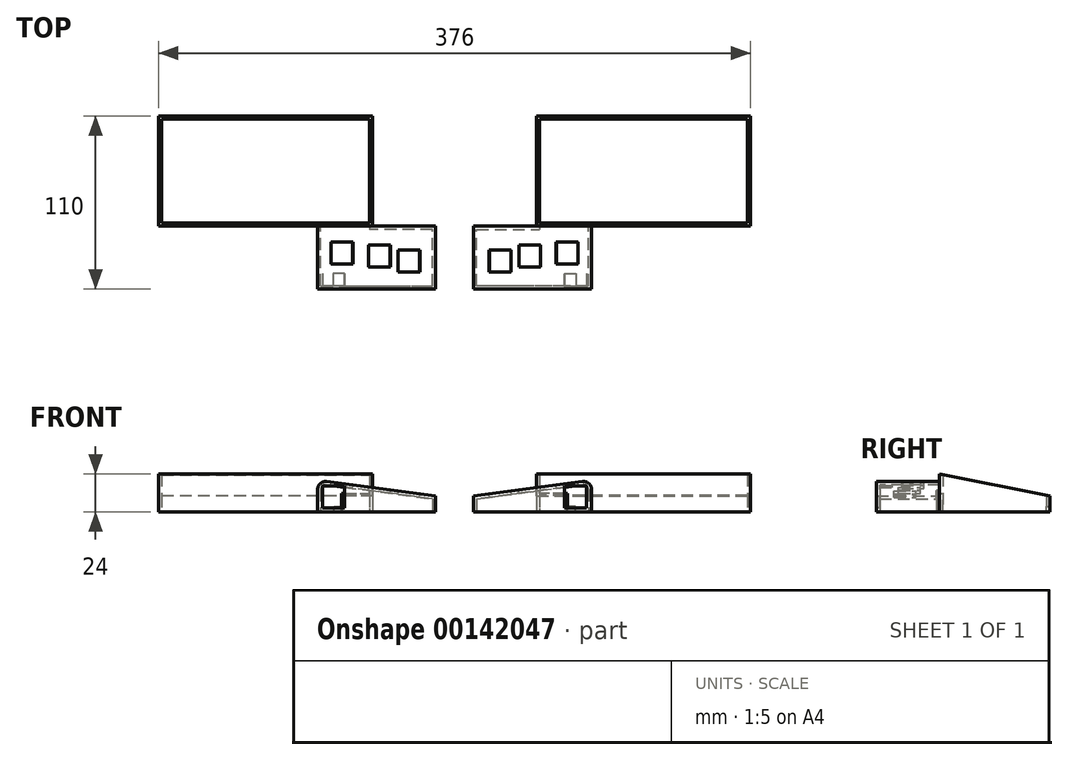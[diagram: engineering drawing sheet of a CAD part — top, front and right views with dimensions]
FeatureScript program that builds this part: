
annotation { "Feature Type Name" : "Feature", "Feature Type Description" : "" }
export const myFeature = defineFeature(function(context is Context, id is Id, definition is map)
    precondition{}
    {
        {
            var Q0;
            Q0=qCreatedBy(makeId("Top.planeOp"),FACE);
            var sketch = newSketch(context, id + "F0", { "sketchPlane" : qUnion([Q0])});
            skLineSegment(sketch, "E0.bottom", {"start": v(68, -35) * mm, "end": v(-68, -35) * mm});
            skLineSegment(sketch, "E0.top", {"start": v(68, 35) * mm, "end": v(-68, 35) * mm});
            skLineSegment(sketch, "E0.left", {"start": v(68, -35) * mm, "end": v(68, 35) * mm});
            skLineSegment(sketch, "E0.right", {"start": v(-68, -35) * mm, "end": v(-68, 35) * mm});
            skPoint(sketch, "E0.middle", {"position": v(0, 0) * mm});
            skLineSegment(sketch, "E1.bottom", {"start": v(-66, 35) * mm, "end": v(66, 35) * mm});
            skLineSegment(sketch, "E1.top", {"start": v(-66, -33) * mm, "end": v(66, -33) * mm});
            skLineSegment(sketch, "E1.left", {"start": v(-66, 35) * mm, "end": v(-66, -33) * mm});
            skLineSegment(sketch, "E1.right", {"start": v(66, 35) * mm, "end": v(66, -33) * mm});
            skLineSegment(sketch, "E2", {"start": v(-68, 4.76) * mm, "end": v(-66, 4.76) * mm});
            skPoint(sketch, "E2.endSnap0", {"position": v(-66, 1) * mm});
            skLineSegment(sketch, "E3", {"start": v(-7.66, -35) * mm, "end": v(-7.66, -33) * mm});
            skLineSegment(sketch, "E4", {"start": v(66, 1) * mm, "end": v(68, 1) * mm});
            skLineSegment(sketch, "E5", {"start": v(-66, 33) * mm, "end": v(66, 33) * mm});
            skLineSegment(sketch, "E6", {"start": v(0, 35) * mm, "end": v(0, 33) * mm});
            skLineSegment(sketch, "E7", {"start": v(-81.81, -13.23) * mm, "end": v(-79.54, -15.2) * mm});
            skLineSegment(sketch, "E8", {"start": v(-140.33, 40.9) * mm, "end": v(-140.33, -57.97) * mm});
            skSolve(sketch);
        }
        {
            var Q0;
            {var subQ3=sQuery(id+"F0.wireOp",EDGE,"E2");Q0=makeQuery(id+"F0.imprint","IMPRINT",FACE,{"disambiguationData":[TD([[makeQuery(id+"F0.imprint","IMPRINT",EDGE,{"derivedFrom":subQ3}),-1.0]])]});}
            var Q1;
            {var subQ5=sQuery(id+"F0.wireOp",EDGE,"E2");Q1=makeQuery(id+"F0.imprint","IMPRINT",FACE,{"disambiguationData":[TD([[makeQuery(id+"F0.imprint","IMPRINT",EDGE,{"derivedFrom":subQ5}),1.0]])]});}
            var Q2;
            {var subQ4=sQuery(id+"F0.wireOp",EDGE,"E3");Q2=makeQuery(id+"F0.imprint","IMPRINT",FACE,{"disambiguationData":[TD([[makeQuery(id+"F0.imprint","IMPRINT",EDGE,{"derivedFrom":subQ4}),-1.0]])]});}
            var Q3;
            {var subQ5=sQuery(id+"F0.wireOp",EDGE,"E4");Q3=makeQuery(id+"F0.imprint","IMPRINT",FACE,{"disambiguationData":[TD([[makeQuery(id+"F0.imprint","IMPRINT",EDGE,{"derivedFrom":subQ5}),1.0]])]});}
            var Q4;
            {var subQ3=sQuery(id+"F0.wireOp",EDGE,"E6");Q4=makeQuery(id+"F0.imprint","IMPRINT",FACE,{"disambiguationData":[TD([[makeQuery(id+"F0.imprint","IMPRINT",EDGE,{"derivedFrom":subQ3}),-1.0]])]});}
            var Q5;
            {var subQ3=sQuery(id+"F0.wireOp",EDGE,"E6");Q5=makeQuery(id+"F0.imprint","IMPRINT",FACE,{"disambiguationData":[TD([[makeQuery(id+"F0.imprint","IMPRINT",EDGE,{"derivedFrom":subQ3}),1.0]])]});}
            extrude(context, id + "F1", {"entities" : qUnion([Q0, Q1, Q2, Q3, Q4, Q5]), "depth" : 24 * mm});
        }
        {
            var Q0;
            Q0=makeQuery(id+"F1.opExtrude","SWEPT_FACE",FACE,{"disambiguationData":[OSD([sQuery(id+"F0.wireOp",EDGE,"E0.left")])]});
            var sketch = newSketch(context, id + "F2", { "sketchPlane" : qUnion([Q0])});
            skLineSegment(sketch, "E9", {"start": v(35, 24) * mm, "end": v(-35, 24) * mm});
            skLineSegment(sketch, "E10", {"start": v(35, 0) * mm, "end": v(35, 10) * mm});
            skLineSegment(sketch, "E11", {"start": v(-35, 24) * mm, "end": v(35, 10) * mm});
            skLineSegment(sketch, "E12", {"start": v(35, 10) * mm, "end": v(35, 24) * mm});
            skSolve(sketch);
        }
        {
            var Q0;
            Q0 = qSketchRegion(id + "F2", true);
            extrude(context, id + "F3", {"entities" : qUnion([Q0]), "operationType" : NewBodyOperationType.REMOVE, "endBound" : BoundingType.THROUGH_ALL, "oppositeDirection" : true, "depth" : 100 * mm});
        }
        {
            var Q0;
            Q0=qCreatedBy(makeId("Top.planeOp"),FACE);
            var sketch = newSketch(context, id + "F4", { "sketchPlane" : qUnion([Q0])});
            skLineSegment(sketch, "E13", {"start": v(-33, -35) * mm, "end": v(-108, -35) * mm});
            skLineSegment(sketch, "E14", {"start": v(-108, -35) * mm, "end": v(-108, -75) * mm});
            skLineSegment(sketch, "E15", {"start": v(-33, -35) * mm, "end": v(-33, -75) * mm});
            skLineSegment(sketch, "E16", {"start": v(-33, -75) * mm, "end": v(-108, -75) * mm});
            skLineSegment(sketch, "E17", {"start": v(-68, -29.84) * mm, "end": v(-68, -41.73) * mm});
            skLineSegment(sketch, "E18", {"start": v(-68, -41.73) * mm, "end": v(-33, -41.73) * mm});
            skSolve(sketch);
        }
        {
            var Q0;
            Q0 = qSketchRegion(id + "F4", true);
            extrude(context, id + "F5", {"entities" : qUnion([Q0]), "operationType" : NewBodyOperationType.ADD, "depth" : 20 * mm});
        }
        {
            var Q0;
            Q0=makeQuery(id+"F5.opExtrude","SWEPT_FACE",FACE,{"disambiguationData":[OSD([sQuery(id+"F4.wireOp",EDGE,"E13")])]});
            var sketch = newSketch(context, id + "F6", { "sketchPlane" : qUnion([Q0])});
            skLineSegment(sketch, "E19", {"start": v(108, 10) * mm, "end": v(108, 0) * mm});
            skLineSegment(sketch, "E20", {"start": v(108, 10) * mm, "end": v(33, 20) * mm});
            skLineSegment(sketch, "E21", {"start": v(108, 0) * mm, "end": v(108, 10) * mm});
            skLineSegment(sketch, "E22", {"start": v(108, 0) * mm, "end": v(33, 0) * mm});
            skLineSegment(sketch, "E23", {"start": v(33, 0) * mm, "end": v(33, 20) * mm});
            skLineSegment(sketch, "E24", {"start": v(108, 20) * mm, "end": v(108, 10) * mm});
            skLineSegment(sketch, "E25", {"start": v(108, 20) * mm, "end": v(33, 20) * mm});
            skSolve(sketch);
        }
        {
            var Q0;
            {var subQ0=sQuery(id+"F6.wireOp",EDGE,"E24");Q0=makeQuery(id+"F6.imprint","IMPRINT",FACE,{"disambiguationData":[TD([[makeQuery(id+"F6.imprint","IMPRINT",EDGE,{"derivedFrom":subQ0}),-1.0]])]});}
            var Q1;
            {var subQ0=sQuery(id+"F6.wireOp",EDGE,"E25");var subQ1=sQuery(id+"F6.wireOp",EDGE,"E20");var subQ2=makeQuery(id+"F6.imprint","INTERSECT",VERTEX,{"derivedFrom":[subQ1,sQuery(id+"F6.wireOp",EDGE,"E23"),subQ0]});Q1=makeQuery(id+"F6.imprint","IMPRINT",FACE,{"disambiguationData":[TD([[makeQuery(id+"F6.imprint","IMPRINT",EDGE,{"disambiguationData":[TD([[subQ2,1.0]])],"derivedFrom":subQ1}),-1.0]])]});}
            extrude(context, id + "F7", {"entities" : qUnion([Q0, Q1]), "operationType" : NewBodyOperationType.REMOVE, "endBound" : BoundingType.THROUGH_ALL, "oppositeDirection" : true, "depth" : 25 * mm});
        }
        {
            var Q0;
            Q0=makeQuery(id+"F7.boolean.opBoolean","MERGE",EDGE,{"derivedFrom":[makeQuery(id+"F5.opExtrude","CAP_EDGE",EDGE,{"disambiguationData":[OSD([sQuery(id+"F4.wireOp",EDGE,"E15")])],"isStart":false}),makeQuery(id+"F7.opExtrude","SWEPT_EDGE",EDGE,{"disambiguationData":[OSD([sQuery(id+"F6.wireOp",EDGE,"E20"),sQuery(id+"F6.wireOp",EDGE,"E23"),sQuery(id+"F6.wireOp",EDGE,"E25")])]})]});
            fillet(context, id + "F8", {"entities" : qUnion([Q0]), "radius" : 5 * mm, "tangentPropagation" : true, "allowEdgeOverflow" : false});
        }
        {
            var Q0;
            Q0=makeQuery(id+"F7.boolean.opBoolean","COPY",FACE,{"derivedFrom":makeQuery(id+"F7.opExtrude","SWEPT_FACE",FACE,{"disambiguationData":[OSD([sQuery(id+"F6.wireOp",EDGE,"E20")])]})});
            var sketch = newSketch(context, id + "F9", { "sketchPlane" : qUnion([Q0])});
            skLineSegment(sketch, "E26.bottom", {"start": v(-52.73, -59) * mm, "end": v(-52.73, -45) * mm});
            skLineSegment(sketch, "E26.top", {"start": v(-38.73, -59) * mm, "end": v(-38.73, -45) * mm});
            skLineSegment(sketch, "E26.left", {"start": v(-52.73, -59) * mm, "end": v(-38.73, -59) * mm});
            skLineSegment(sketch, "E26.right", {"start": v(-52.73, -45) * mm, "end": v(-38.73, -45) * mm});
            skPoint(sketch, "E26.middle", {"position": v(-45.73, -52) * mm});
            skLineSegment(sketch, "E27.bottom", {"start": v(-76.73, -61) * mm, "end": v(-76.73, -47) * mm});
            skLineSegment(sketch, "E27.top", {"start": v(-62.73, -61) * mm, "end": v(-62.73, -47) * mm});
            skLineSegment(sketch, "E27.left", {"start": v(-76.73, -61) * mm, "end": v(-62.73, -61) * mm});
            skLineSegment(sketch, "E27.right", {"start": v(-76.73, -47) * mm, "end": v(-62.73, -47) * mm});
            skPoint(sketch, "E27.middle", {"position": v(-69.73, -54) * mm});
            skLineSegment(sketch, "E28", {"start": v(-62.73, -54) * mm, "end": v(-52.73, -54) * mm});
            skLineSegment(sketch, "E29.bottom", {"start": v(-95.73, -64) * mm, "end": v(-95.73, -50) * mm});
            skLineSegment(sketch, "E29.top", {"start": v(-81.73, -64) * mm, "end": v(-81.73, -50) * mm});
            skLineSegment(sketch, "E29.left", {"start": v(-95.73, -64) * mm, "end": v(-81.73, -64) * mm});
            skLineSegment(sketch, "E29.right", {"start": v(-95.73, -50) * mm, "end": v(-81.73, -50) * mm});
            skPoint(sketch, "E29.middle", {"position": v(-88.73, -57) * mm});
            skLineSegment(sketch, "E30", {"start": v(-81.73, -57) * mm, "end": v(-76.73, -57) * mm});
            skLineSegment(sketch, "E31", {"start": v(-35.72, -45) * mm, "end": v(-35.78, -35) * mm});
            skLineSegment(sketch, "E32", {"start": v(-69.73, -47) * mm, "end": v(-69.73, -35) * mm});
            skLineSegment(sketch, "E33", {"start": v(-85.55, -35) * mm, "end": v(-85.55, -50) * mm});
            skPoint(sketch, "E33.endSnap0", {"position": v(-88.73, -50) * mm});
            skLineSegment(sketch, "E34", {"start": v(-95.73, -57) * mm, "end": v(-105.73, -57) * mm});
            skSolve(sketch);
        }
        {
            var Q0;
            Q0=makeQuery(id+"F5.boolean.opBoolean","MERGE",FACE,{"derivedFrom":[makeQuery(id+"F1.opExtrude","CAP_FACE",FACE,{"disambiguationData":[OSD([sQuery(id+"F0.wireOp",EDGE,"E0.bottom"),sQuery(id+"F0.wireOp",EDGE,"E0.top"),sQuery(id+"F0.wireOp",EDGE,"E0.left"),sQuery(id+"F0.wireOp",EDGE,"E0.right"),sQuery(id+"F0.wireOp",EDGE,"E1.bottom"),sQuery(id+"F0.wireOp",EDGE,"E1.top"),sQuery(id+"F0.wireOp",EDGE,"E1.left"),sQuery(id+"F0.wireOp",EDGE,"E1.right"),sQuery(id+"F0.wireOp",EDGE,"E5")])],"isStart":true}),makeQuery(id+"F5.opExtrude","CAP_FACE",FACE,{"disambiguationData":[OSD([sQuery(id+"F4.wireOp",EDGE,"E13"),sQuery(id+"F4.wireOp",EDGE,"E14"),sQuery(id+"F4.wireOp",EDGE,"E15"),sQuery(id+"F4.wireOp",EDGE,"E16")])],"isStart":true})]});
            var Q1;
            Q1=makeQuery(id+"F1.opExtrude","SWEPT_BODY",BODY,{"disambiguationData":[OSD([sQuery(id+"F0.wireOp",EDGE,"E0.bottom"),sQuery(id+"F0.wireOp",EDGE,"E0.top"),sQuery(id+"F0.wireOp",EDGE,"E0.left"),sQuery(id+"F0.wireOp",EDGE,"E0.right"),sQuery(id+"F0.wireOp",EDGE,"E1.bottom"),sQuery(id+"F0.wireOp",EDGE,"E1.top"),sQuery(id+"F0.wireOp",EDGE,"E1.left"),sQuery(id+"F0.wireOp",EDGE,"E1.right"),sQuery(id+"F0.wireOp",EDGE,"E5")])]});
            shell(context, id + "F10", {"entities" : qUnion([Q0]), "parts" : qUnion([Q1]), "thickness" : 2 * mm});
        }
        {
            var Q0;
            Q0 = qSketchRegion(id + "F9", true);
            extrude(context, id + "F11", {"entities" : qUnion([Q0]), "operationType" : NewBodyOperationType.REMOVE, "oppositeDirection" : true, "depth" : 25 * mm});
        }
        {
            var Q0;
            Q0=makeQuery(id+"F1.opExtrude","SWEPT_FACE",FACE,{"disambiguationData":[OSD([sQuery(id+"F0.wireOp",EDGE,"E0.top"),sQuery(id+"F0.wireOp",EDGE,"E1.bottom")])]});
            var sketch = newSketch(context, id + "F12", { "sketchPlane" : qUnion([Q0])});
            skLineSegment(sketch, "E35.bottom", {"start": v(43.3, 0) * mm, "end": v(48.68, 0) * mm});
            skLineSegment(sketch, "E35.top", {"start": v(43.3, 3.62) * mm, "end": v(48.68, 3.62) * mm});
            skLineSegment(sketch, "E35.left", {"start": v(43.3, 0) * mm, "end": v(43.3, 3.62) * mm});
            skLineSegment(sketch, "E35.right", {"start": v(48.68, 0) * mm, "end": v(48.68, 3.62) * mm});
            skSolve(sketch);
        }
        {
            var Q0;
            Q0=makeQuery(id+"F12.imprint","IMPRINT",FACE,{"disambiguationData":[TD([[makeQuery(id+"F12.imprint","IMPRINT",EDGE,{"derivedFrom":sQuery(id+"F12.wireOp",EDGE,"E35.bottom")}),1.0]])]});
            extrude(context, id + "F13", {"entities" : qUnion([Q0]), "operationType" : NewBodyOperationType.REMOVE, "oppositeDirection" : true, "depth" : 5 * mm});
        }
        {
            var Q0;
            Q0=makeQuery(id+"F1.opExtrude","SWEPT_FACE",FACE,{"disambiguationData":[OSD([sQuery(id+"F0.wireOp",EDGE,"E1.top")])]});
            var sketch = newSketch(context, id + "F14", { "sketchPlane" : qUnion([Q0])});
            skLineSegment(sketch, "E36.bottom", {"start": v(48.31, 0) * mm, "end": v(66, 0) * mm});
            skLineSegment(sketch, "E36.top", {"start": v(48.31, 11.8) * mm, "end": v(66, 11.8) * mm});
            skLineSegment(sketch, "E36.left", {"start": v(48.31, 0) * mm, "end": v(48.31, 11.8) * mm});
            skLineSegment(sketch, "E36.right", {"start": v(66, 0) * mm, "end": v(66, 11.8) * mm});
            skSolve(sketch);
        }
        {
            var Q0;
            Q0 = qSketchRegion(id + "F14", true);
            extrude(context, id + "F15", {"entities" : qUnion([Q0]), "operationType" : NewBodyOperationType.REMOVE, "oppositeDirection" : true, "depth" : 10 * mm});
        }
        {
            var Q0;
            Q0=qCreatedBy(makeId("Right.planeOp"),FACE);
            cPlane(context, id + "F16", {"entities" : qUnion([Q0]), "cplaneType" : CPlaneType.OFFSET, "offset" : 120 * mm, "oppositeDirection" : true, "width" : 150 * mm, "height" : 150 * mm});
        }
        {
            var Q0;
            Q0=makeQuery(id+"F5.opExtrude","SWEPT_FACE",FACE,{"disambiguationData":[OSD([sQuery(id+"F4.wireOp",EDGE,"E16")])]});
            var sketch = newSketch(context, id + "F17", { "sketchPlane" : qUnion([Q0])});
            skLineSegment(sketch, "E37.bottom", {"start": v(-50.09, 2.65) * mm, "end": v(-50.09, 16.65) * mm});
            skLineSegment(sketch, "E37.top", {"start": v(-36.09, 2.65) * mm, "end": v(-36.09, 16.65) * mm});
            skLineSegment(sketch, "E37.left", {"start": v(-50.09, 2.65) * mm, "end": v(-36.09, 2.65) * mm});
            skLineSegment(sketch, "E37.right", {"start": v(-50.09, 16.65) * mm, "end": v(-36.09, 16.65) * mm});
            skPoint(sketch, "E37.middle", {"position": v(-43.09, 9.65) * mm});
            skLineSegment(sketch, "E38", {"start": v(-43.09, 16.65) * mm, "end": v(-43.09, 18.65) * mm});
            skSolve(sketch);
        }
        {
            var Q0;
            Q0=makeQuery(id+"F17.imprint","IMPRINT",FACE,{"disambiguationData":[TD([[makeQuery(id+"F17.imprint","IMPRINT",EDGE,{"derivedFrom":sQuery(id+"F17.wireOp",EDGE,"E37.bottom")}),-1.0]])]});
            extrude(context, id + "F18", {"entities" : qUnion([Q0]), "operationType" : NewBodyOperationType.REMOVE, "oppositeDirection" : true, "depth" : 10 * mm});
        }
        {
            var Q0;
            Q0=makeQuery(id+"F1.opExtrude","SWEPT_BODY",BODY,{"disambiguationData":[OSD([sQuery(id+"F0.wireOp",EDGE,"E0.bottom"),sQuery(id+"F0.wireOp",EDGE,"E0.top"),sQuery(id+"F0.wireOp",EDGE,"E0.left"),sQuery(id+"F0.wireOp",EDGE,"E0.right"),sQuery(id+"F0.wireOp",EDGE,"E1.bottom"),sQuery(id+"F0.wireOp",EDGE,"E1.top"),sQuery(id+"F0.wireOp",EDGE,"E1.left"),sQuery(id+"F0.wireOp",EDGE,"E1.right"),sQuery(id+"F0.wireOp",EDGE,"E5")])]});
            var Q1;
            Q1=qCreatedBy(id+"F16.planeOp",FACE);
            mirror(context, id + "F19", {"entities" : qUnion([Q0]), "mirrorPlane" : qUnion([Q1])});
        }
    });
